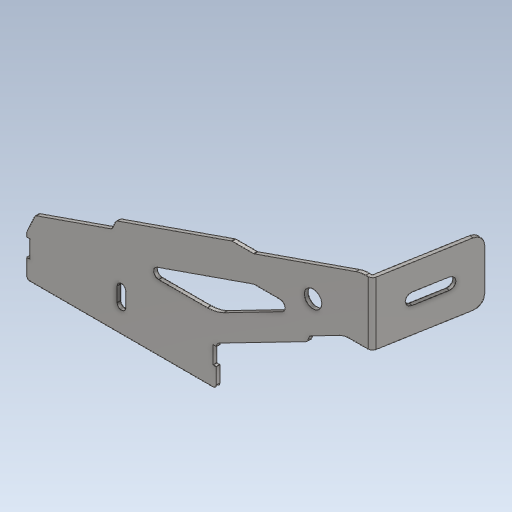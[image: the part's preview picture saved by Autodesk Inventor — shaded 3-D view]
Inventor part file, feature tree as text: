
AUTODESK INVENTOR PART (.ipt)
format: ipt  version: 2020 (Build 240168000, 168)  size: 591,360 bytes
history: native  units: mm
features: other x3, extrude x1, plane x1
ambient origin geometry x8: Origin, YZ Plane, XZ Plane, XY Plane, X Axis, Y Axis, Z Axis, Center Point
bodies: Body1 (feature_tree)
feature tree (5):
  other  "實體1"
  extrude  "擠出1"  Depth=130.0mm
  other  "折彎零件1"
  plane  "工作平面1"
  other  "定義1"
